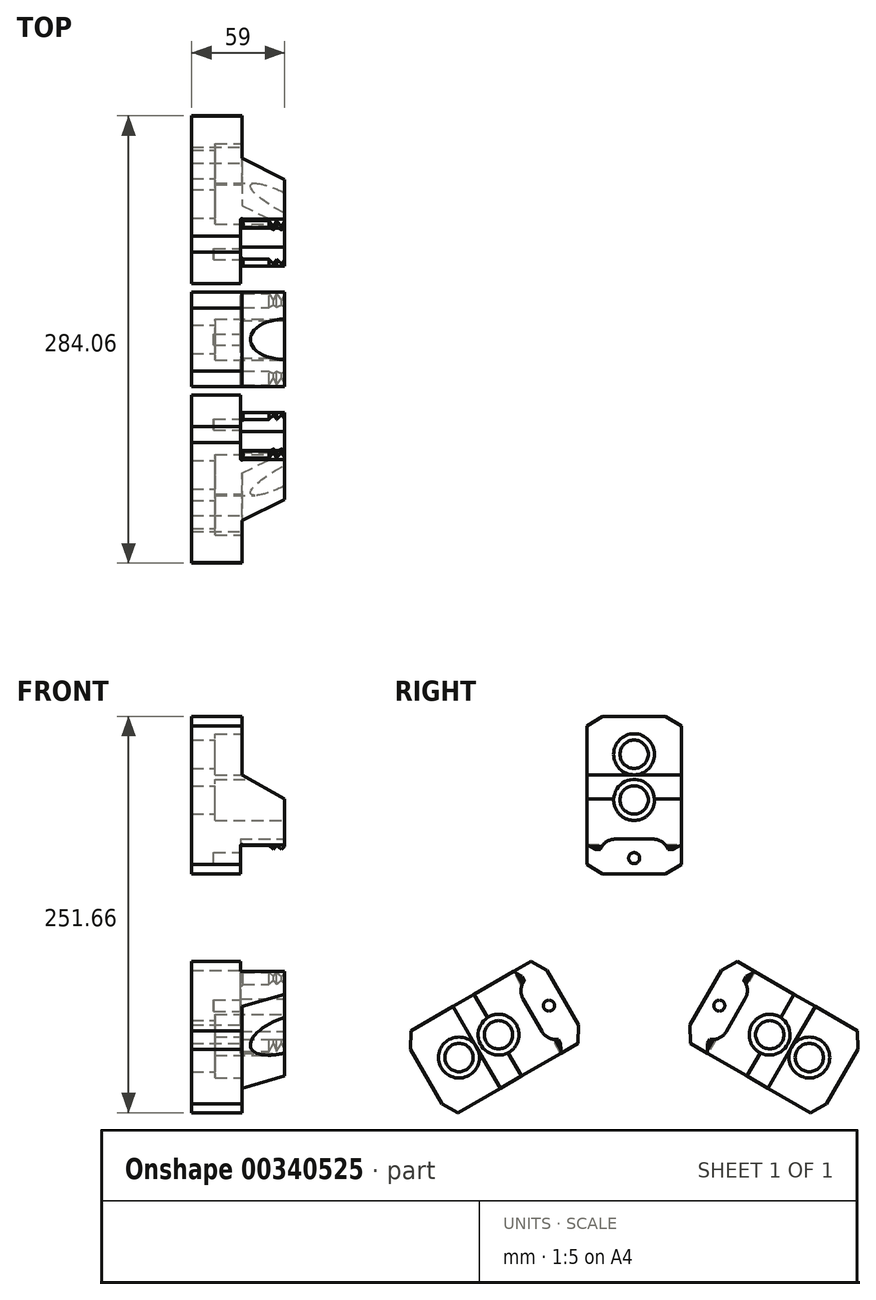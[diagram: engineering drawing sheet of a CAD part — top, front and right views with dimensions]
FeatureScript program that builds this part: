
annotation { "Feature Type Name" : "Feature", "Feature Type Description" : "" }
export const myFeature = defineFeature(function(context is Context, id is Id, definition is map)
    precondition{}
    {
        {
            var Q0;
            Q0=qCreatedBy(makeId("Front.planeOp"),FACE);
            var sketch = newSketch(context, id + "F0", { "sketchPlane" : qUnion([Q0])});
            skLineSegment(sketch, "E0", {"start": v(3, 52.45) * mm, "end": v(3, 152.45) * mm});
            skLineSegment(sketch, "E1", {"start": v(3, 152.45) * mm, "end": v(35, 152.45) * mm});
            skLineSegment(sketch, "E2", {"start": v(35, 152.45) * mm, "end": v(35, 115.45) * mm});
            skLineSegment(sketch, "E3", {"start": v(35, 115.45) * mm, "end": v(62, 100) * mm});
            skLineSegment(sketch, "E4", {"start": v(62, 100) * mm, "end": v(62, 70) * mm});
            skLineSegment(sketch, "E5", {"start": v(3, 52.45) * mm, "end": v(34, 52.45) * mm});
            skLineSegment(sketch, "E6", {"start": v(34, 52.45) * mm, "end": v(34, 70.45) * mm});
            skLineSegment(sketch, "E7", {"start": v(52, 70.45) * mm, "end": v(55, 68) * mm});
            skLineSegment(sketch, "E8", {"start": v(55, 68) * mm, "end": v(57, 70.45) * mm});
            skLineSegment(sketch, "E9", {"start": v(57, 70.45) * mm, "end": v(60, 68) * mm});
            skLineSegment(sketch, "E10", {"start": v(60, 68) * mm, "end": v(62, 70) * mm});
            skArc(sketch, "E11", {"start": v(35.5, 70.45) * mm, "mid": v(34.75, 71.2) * mm, "end": v(34, 70.45) * mm});
            skLineSegment(sketch, "E12.trimOffspring", {"start": v(35.5, 70.45) * mm, "end": v(52, 70.45) * mm});
            skLineSegment(sketch, "E13", {"start": v(0, 0) * mm, "end": v(70.08, 0) * mm, "construction": true});
            skSolve(sketch);
        }
        {
            var Q0;
            Q0=qSketchRegion(id+"F0",true);
            extrude(context, id + "F1", {"entities" : qUnion([Q0]), "endBound" : BoundingType.SYMMETRIC, "depth" : 60 * mm});
        }
        {
            var Q0;
            Q0=makeQuery(id+"F1.opExtrude","SWEPT_FACE",FACE,{"disambiguationData":[OSD([sQuery(id+"F0.wireOp",EDGE,"E2")])]});
            var sketch = newSketch(context, id + "F2", { "sketchPlane" : qUnion([Q0])});
            skLineSegment(sketch, "E14", {"start": v(20, 152.45) * mm, "end": v(30, 146.45) * mm});
            skLineSegment(sketch, "E15", {"start": v(30, 146.45) * mm, "end": v(30, 152.45) * mm});
            skLineSegment(sketch, "E16", {"start": v(30, 152.45) * mm, "end": v(20, 152.45) * mm});
            skLineSegment(sketch, "E17", {"start": v(20, 52.45) * mm, "end": v(30, 58.45) * mm});
            skLineSegment(sketch, "E18", {"start": v(30, 58.45) * mm, "end": v(30, 52.45) * mm});
            skLineSegment(sketch, "E19", {"start": v(30, 52.45) * mm, "end": v(20, 52.45) * mm});
            skLineSegment(sketch, "E20", {"start": v(0, 42.7) * mm, "end": v(0, 168.17) * mm, "construction": true});
            skLineSegment(sketch, "E21.MirrorCS", {"start": v(-20, 152.45) * mm, "end": v(-30, 146.45) * mm});
            skLineSegment(sketch, "E22.MirrorCS", {"start": v(-30, 152.45) * mm, "end": v(-20, 152.45) * mm});
            skLineSegment(sketch, "E23.MirrorCS", {"start": v(-30, 146.45) * mm, "end": v(-30, 152.45) * mm});
            skLineSegment(sketch, "E24.MirrorCS", {"start": v(-20, 52.45) * mm, "end": v(-30, 58.45) * mm});
            skLineSegment(sketch, "E25.MirrorCS", {"start": v(-30, 58.45) * mm, "end": v(-30, 52.45) * mm});
            skLineSegment(sketch, "E26.MirrorCS", {"start": v(-30, 52.45) * mm, "end": v(-20, 52.45) * mm});
            skSolve(sketch);
        }
        {
            var Q0;
            Q0=makeQuery(id+"F2.imprint","IMPRINT",FACE,{"disambiguationData":[TD([[makeQuery(id+"F2.imprint","IMPRINT",EDGE,{"derivedFrom":sQuery(id+"F2.wireOp",EDGE,"E21.MirrorCS")}),-1.0]])]});
            var Q1;
            Q1=makeQuery(id+"F2.imprint","IMPRINT",FACE,{"disambiguationData":[TD([[makeQuery(id+"F2.imprint","IMPRINT",EDGE,{"derivedFrom":sQuery(id+"F2.wireOp",EDGE,"E14")}),1.0]])]});
            var Q2;
            Q2=makeQuery(id+"F2.imprint","IMPRINT",FACE,{"disambiguationData":[TD([[makeQuery(id+"F2.imprint","IMPRINT",EDGE,{"derivedFrom":sQuery(id+"F2.wireOp",EDGE,"E17")}),-1.0]])]});
            var Q3;
            Q3=makeQuery(id+"F2.imprint","IMPRINT",FACE,{"disambiguationData":[TD([[makeQuery(id+"F2.imprint","IMPRINT",EDGE,{"derivedFrom":sQuery(id+"F2.wireOp",EDGE,"E24.MirrorCS")}),1.0]])]});
            var Q4;
            Q4=makeQuery(id+"F1.opExtrude","SWEPT_FACE",FACE,{"disambiguationData":[OSD([sQuery(id+"F0.wireOp",EDGE,"E0")])]});
            extrude(context, id + "F3", {"entities" : qUnion([Q0, Q1, Q2, Q3]), "operationType" : NewBodyOperationType.REMOVE, "endBound" : BoundingType.UP_TO_SURFACE, "oppositeDirection" : true, "endBoundEntityFace" : qUnion([Q4]), "depth" : 25 * mm});
        }
        {
            var Q0;
            Q0=makeQuery(id+"F1.opExtrude","SWEPT_FACE",FACE,{"disambiguationData":[OSD([sQuery(id+"F0.wireOp",EDGE,"E4")])]});
            var sketch = newSketch(context, id + "F4", { "sketchPlane" : qUnion([Q0])});
            skLineSegment(sketch, "E27", {"start": v(30, 71) * mm, "end": v(24.5, 68) * mm});
            skLineSegment(sketch, "E28", {"start": v(24.5, 68) * mm, "end": v(30, 68) * mm});
            skLineSegment(sketch, "E29", {"start": v(30, 68) * mm, "end": v(30, 71) * mm});
            skLineSegment(sketch, "E30", {"start": v(0, 67.05) * mm, "end": v(0, 113.15) * mm, "construction": true});
            skPoint(sketch, "E30.endSnap0", {"position": v(0, 100) * mm});
            skLineSegment(sketch, "E31.MirrorCS", {"start": v(-30, 71) * mm, "end": v(-24.5, 68) * mm});
            skLineSegment(sketch, "E32.MirrorCS", {"start": v(-30, 68) * mm, "end": v(-30, 71) * mm});
            skLineSegment(sketch, "E33.MirrorCS", {"start": v(-24.5, 68) * mm, "end": v(-30, 68) * mm});
            skSolve(sketch);
        }
        {
            var Q0;
            {var subQ0=sQuery(id+"F4.wireOp",EDGE,"E33.MirrorCS");Q0=makeQuery(id+"F4.imprint","IMPRINT",FACE,{"disambiguationData":[TD([[makeQuery(id+"F4.imprint","IMPRINT",EDGE,{"derivedFrom":subQ0}),-1.0]])]});}
            var Q1;
            {var subQ0=sQuery(id+"F4.wireOp",EDGE,"E32.MirrorCS");var subQ1=sQuery(id+"F4.wireOp",EDGE,"E31.MirrorCS");var subQ2=sQuery(id+"F0.wireOp",EDGE,"E4");var subQ3=makeQuery(id+"F4.imprint","INTERSECT",VERTEX,{"derivedFrom":[makeQuery(id+"F1.opExtrude","CAP_EDGE",EDGE,{"disambiguationData":[OSD([subQ2])],"isStart":false}),subQ1,subQ0]});Q1=makeQuery(id+"F4.imprint","IMPRINT",FACE,{"disambiguationData":[TD([[makeQuery(id+"F4.imprint","IMPRINT",EDGE,{"disambiguationData":[TD([[subQ3,-1.0]])],"derivedFrom":subQ1}),-1.0]])]});}
            var Q2;
            {var subQ0=sQuery(id+"F4.wireOp",EDGE,"E29");var subQ1=sQuery(id+"F4.wireOp",EDGE,"E27");var subQ2=sQuery(id+"F0.wireOp",EDGE,"E4");var subQ3=makeQuery(id+"F4.imprint","INTERSECT",VERTEX,{"derivedFrom":[makeQuery(id+"F1.opExtrude","CAP_EDGE",EDGE,{"disambiguationData":[OSD([subQ2])],"isStart":true}),subQ1,subQ0]});Q2=makeQuery(id+"F4.imprint","IMPRINT",FACE,{"disambiguationData":[TD([[makeQuery(id+"F4.imprint","IMPRINT",EDGE,{"disambiguationData":[TD([[subQ3,-1.0]])],"derivedFrom":subQ1}),1.0]])]});}
            var Q3;
            {var subQ0=sQuery(id+"F4.wireOp",EDGE,"E28");Q3=makeQuery(id+"F4.imprint","IMPRINT",FACE,{"disambiguationData":[TD([[makeQuery(id+"F4.imprint","IMPRINT",EDGE,{"derivedFrom":subQ0}),1.0]])]});}
            var Q4;
            Q4=makeQuery(id+"F1.opExtrude","SWEPT_FACE",FACE,{"disambiguationData":[OSD([sQuery(id+"F0.wireOp",EDGE,"E6")])]});
            extrude(context, id + "F5", {"entities" : qUnion([Q0, Q1, Q2, Q3]), "operationType" : NewBodyOperationType.REMOVE, "endBound" : BoundingType.UP_TO_SURFACE, "oppositeDirection" : true, "endBoundEntityFace" : qUnion([Q4]), "depth" : 27.7 * mm});
        }
        {
            var Q0;
            Q0=makeQuery(id+"F1.opExtrude","SWEPT_FACE",FACE,{"disambiguationData":[OSD([sQuery(id+"F0.wireOp",EDGE,"E4")])]});
            var sketch = newSketch(context, id + "F6", { "sketchPlane" : qUnion([Q0])});
            skLineSegment(sketch, "E34", {"start": v(0, 70.5) * mm, "end": v(0, 96.88) * mm, "construction": true});
            skPoint(sketch, "E34.startSnap0", {"position": v(0, 70) * mm});
            skLineSegment(sketch, "E35", {"start": v(12.26, 74.5) * mm, "end": v(0, 74.5) * mm});
            skLineSegment(sketch, "E36", {"start": v(21.5, 68) * mm, "end": v(0, 68) * mm});
            skPoint(sketch, "E37", {"position": v(12, 74.5) * mm});
            skArc(sketch, "E38", {"start": v(21.5, 68) * mm, "mid": v(17.78, 72.75) * mm, "end": v(12, 74.5) * mm});
            skPoint(sketch, "E39.end.orphan", {"position": v(21.5, 74.5) * mm});
            skLineSegment(sketch, "E40.MirrorCS", {"start": v(-12.26, 74.5) * mm, "end": v(0, 74.5) * mm});
            skArc(sketch, "E41.MirrorCS", {"start": v(-21.5, 68) * mm, "mid": v(-17.78, 72.75) * mm, "end": v(-12, 74.5) * mm});
            skLineSegment(sketch, "E42.MirrorCS", {"start": v(-21.5, 68) * mm, "end": v(0, 68) * mm});
            skSolve(sketch);
        }
        {
            var Q0;
            Q0=qSketchRegion(id+"F6",true);
            var Q1;
            {var subQ0=sQuery(id+"F0.wireOp",EDGE,"E6");Q1=makeQuery(id+"F5.boolean.opBoolean","MERGE",FACE,{"derivedFrom":[makeQuery(id+"F1.opExtrude","SWEPT_FACE",FACE,{"disambiguationData":[OSD([subQ0])]}),makeQuery(id+"F5.opExtrude","CAP_FACE",FACE,{"disambiguationData":[OSD([subQ0]),ownerDisambiguation([makeQuery(id+"F5.opExtrude","SWEPT_BODY",BODY,{"disambiguationData":[OSD([sQuery(id+"F4.wireOp",EDGE,"E27"),sQuery(id+"F4.wireOp",EDGE,"E28"),sQuery(id+"F4.wireOp",EDGE,"E29")])]})])],"isStart":false}),makeQuery(id+"F5.opExtrude","CAP_FACE",FACE,{"disambiguationData":[OSD([subQ0]),ownerDisambiguation([makeQuery(id+"F5.opExtrude","SWEPT_BODY",BODY,{"disambiguationData":[OSD([sQuery(id+"F4.wireOp",EDGE,"E31.MirrorCS"),sQuery(id+"F4.wireOp",EDGE,"E32.MirrorCS"),sQuery(id+"F4.wireOp",EDGE,"E33.MirrorCS")])]})])],"isStart":false})]});}
            extrude(context, id + "F7", {"entities" : qUnion([Q0]), "operationType" : NewBodyOperationType.REMOVE, "endBound" : BoundingType.UP_TO_SURFACE, "oppositeDirection" : true, "endBoundEntityFace" : qUnion([Q1]), "depth" : 25 * mm});
        }
        {
            var Q0;
            {var subQ0=sQuery(id+"F0.wireOp",EDGE,"E6");Q0=makeQuery(id+"F7.boolean.opBoolean","MERGE",FACE,{"derivedFrom":[makeQuery(id+"F5.boolean.opBoolean","MERGE",FACE,{"derivedFrom":[makeQuery(id+"F1.opExtrude","SWEPT_FACE",FACE,{"disambiguationData":[OSD([subQ0])]}),makeQuery(id+"F5.opExtrude","CAP_FACE",FACE,{"disambiguationData":[OSD([subQ0]),ownerDisambiguation([makeQuery(id+"F5.opExtrude","SWEPT_BODY",BODY,{"disambiguationData":[OSD([sQuery(id+"F4.wireOp",EDGE,"E27"),sQuery(id+"F4.wireOp",EDGE,"E28"),sQuery(id+"F4.wireOp",EDGE,"E29")])]})])],"isStart":false}),makeQuery(id+"F5.opExtrude","CAP_FACE",FACE,{"disambiguationData":[OSD([subQ0]),ownerDisambiguation([makeQuery(id+"F5.opExtrude","SWEPT_BODY",BODY,{"disambiguationData":[OSD([sQuery(id+"F4.wireOp",EDGE,"E31.MirrorCS"),sQuery(id+"F4.wireOp",EDGE,"E32.MirrorCS"),sQuery(id+"F4.wireOp",EDGE,"E33.MirrorCS")])]})])],"isStart":false})]}),makeQuery(id+"F7.opExtrude","CAP_FACE",FACE,{"disambiguationData":[OSD([subQ0])],"isStart":false})]});}
            var sketch = newSketch(context, id + "F8", { "sketchPlane" : qUnion([Q0])});
            skCircle(sketch, "E43.cCircle", {"center": v(0, 62.45) * mm, "radius": 6.5 * mm, "construction": true});
            skLineSegment(sketch, "E43.0", {"start": v(7.5, 62.45) * mm, "end": v(3.75, 55.95) * mm});
            skLineSegment(sketch, "E43.1", {"start": v(3.75, 55.95) * mm, "end": v(-3.75, 55.95) * mm});
            skLineSegment(sketch, "E43.2", {"start": v(-3.75, 55.95) * mm, "end": v(-7.5, 62.45) * mm});
            skLineSegment(sketch, "E43.3", {"start": v(-7.5, 62.45) * mm, "end": v(-3.75, 68.95) * mm});
            skLineSegment(sketch, "E43.4", {"start": v(-3.75, 68.95) * mm, "end": v(3.75, 68.95) * mm});
            skLineSegment(sketch, "E43.5", {"start": v(3.75, 68.95) * mm, "end": v(7.5, 62.45) * mm});
            skPoint(sketch, "E43.0.midPoint", {"position": v(5.63, 59.2) * mm});
            skCircle(sketch, "E44", {"center": v(0, 62.45) * mm, "radius": 3.5 * mm});
            skSolve(sketch);
        }
        {
            var Q0;
            Q0=makeQuery(id+"F8.imprint","IMPRINT",FACE,{"disambiguationData":[TD([[makeQuery(id+"F8.imprint","IMPRINT",EDGE,{"derivedFrom":sQuery(id+"F8.wireOp",EDGE,"E44")}),1.0]])]});
            extrude(context, id + "F9", {"entities" : qUnion([Q0]), "operationType" : NewBodyOperationType.REMOVE, "oppositeDirection" : true, "depth" : 17 * mm});
        }
        {
            var Q0;
            Q0=makeQuery(id+"F1.opExtrude","SWEPT_FACE",FACE,{"disambiguationData":[OSD([sQuery(id+"F0.wireOp",EDGE,"E4")])]});
            var sketch = newSketch(context, id + "F10", { "sketchPlane" : qUnion([Q0])});
            skLineSegment(sketch, "E45", {"start": v(0, 77.6) * mm, "end": v(0, 164.13) * mm, "construction": true});
            skPoint(sketch, "E45.startSnap0", {"position": v(0, 74.5) * mm});
            skCircle(sketch, "E46", {"center": v(0, 128.45) * mm, "radius": 13 * mm});
            skCircle(sketch, "E47", {"center": v(0, 99.45) * mm, "radius": 13 * mm});
            skCircle(sketch, "E48", {"center": v(0, 128.45) * mm, "radius": 9 * mm});
            skCircle(sketch, "E49", {"center": v(0, 99.45) * mm, "radius": 9 * mm});
            skSolve(sketch);
        }
        {
            var Q0;
            Q0=makeQuery(id+"F10.imprint","IMPRINT",FACE,{"disambiguationData":[TD([[makeQuery(id+"F10.imprint","IMPRINT",EDGE,{"derivedFrom":sQuery(id+"F10.wireOp",EDGE,"E48")}),1.0]])]});
            var Q1;
            {var subQ0=sQuery(id+"F10.wireOp",EDGE,"E49");var subQ1=makeQuery(id+"F1.opExtrude","SWEPT_EDGE",EDGE,{"disambiguationData":[OSD([sQuery(id+"F0.wireOp",EDGE,"E3"),sQuery(id+"F0.wireOp",EDGE,"E4")])]});var subQ2=makeQuery(id+"F10.imprint","INTERSECT",VERTEX,{"disambiguationData":[OD(0.0)],"derivedFrom":[subQ1,subQ0]});Q1=makeQuery(id+"F10.imprint","IMPRINT",FACE,{"disambiguationData":[TD([[makeQuery(id+"F10.imprint","IMPRINT",EDGE,{"disambiguationData":[TD([[subQ2,1.0]])],"derivedFrom":subQ0}),1.0]])]});}
            var Q2;
            {var subQ0=sQuery(id+"F10.wireOp",EDGE,"E49");var subQ1=makeQuery(id+"F1.opExtrude","SWEPT_EDGE",EDGE,{"disambiguationData":[OSD([sQuery(id+"F0.wireOp",EDGE,"E3"),sQuery(id+"F0.wireOp",EDGE,"E4")])]});var subQ2=makeQuery(id+"F10.imprint","INTERSECT",VERTEX,{"disambiguationData":[OD(0.0)],"derivedFrom":[subQ1,subQ0]});Q2=makeQuery(id+"F10.imprint","IMPRINT",FACE,{"disambiguationData":[TD([[makeQuery(id+"F10.imprint","IMPRINT",EDGE,{"disambiguationData":[TD([[subQ2,-1.0]])],"derivedFrom":subQ0}),1.0]])]});}
            var Q3;
            Q3=makeQuery(id+"F1.opExtrude","SWEPT_FACE",FACE,{"disambiguationData":[OSD([sQuery(id+"F0.wireOp",EDGE,"E0")])]});
            extrude(context, id + "F11", {"entities" : qUnion([Q0, Q1, Q2]), "operationType" : NewBodyOperationType.REMOVE, "endBound" : BoundingType.UP_TO_SURFACE, "oppositeDirection" : true, "endBoundEntityFace" : qUnion([Q3]), "depth" : 25 * mm});
        }
        {
            var Q0;
            Q0=makeQuery(id+"F10.imprint","IMPRINT",FACE,{"disambiguationData":[TD([[makeQuery(id+"F10.imprint","IMPRINT",EDGE,{"derivedFrom":sQuery(id+"F10.wireOp",EDGE,"E46")}),1.0]])]});
            var Q1;
            {var subQ0=sQuery(id+"F10.wireOp",EDGE,"E47");var subQ1=makeQuery(id+"F1.opExtrude","SWEPT_EDGE",EDGE,{"disambiguationData":[OSD([sQuery(id+"F0.wireOp",EDGE,"E3"),sQuery(id+"F0.wireOp",EDGE,"E4")])]});var subQ2=makeQuery(id+"F10.imprint","INTERSECT",VERTEX,{"disambiguationData":[OD(0.0)],"derivedFrom":[subQ1,subQ0]});Q1=makeQuery(id+"F10.imprint","IMPRINT",FACE,{"disambiguationData":[TD([[makeQuery(id+"F10.imprint","IMPRINT",EDGE,{"disambiguationData":[TD([[subQ2,-1.0]])],"derivedFrom":subQ0}),1.0]])]});}
            var Q2;
            {var subQ0=sQuery(id+"F10.wireOp",EDGE,"E47");var subQ1=makeQuery(id+"F1.opExtrude","SWEPT_EDGE",EDGE,{"disambiguationData":[OSD([sQuery(id+"F0.wireOp",EDGE,"E3"),sQuery(id+"F0.wireOp",EDGE,"E4")])]});var subQ2=makeQuery(id+"F10.imprint","INTERSECT",VERTEX,{"disambiguationData":[OD(0.0)],"derivedFrom":[subQ1,subQ0]});Q2=makeQuery(id+"F10.imprint","IMPRINT",FACE,{"disambiguationData":[TD([[makeQuery(id+"F10.imprint","IMPRINT",EDGE,{"disambiguationData":[TD([[subQ2,1.0]])],"derivedFrom":subQ0}),1.0]])]});}
            extrude(context, id + "F12", {"entities" : qUnion([Q0, Q1, Q2]), "operationType" : NewBodyOperationType.REMOVE, "oppositeDirection" : true, "depth" : 44 * mm});
        }
        {
            var Q0;
            Q0=makeQuery(id+"F1.opExtrude","SWEPT_BODY",BODY,{"disambiguationData":[OSD([sQuery(id+"F0.wireOp",EDGE,"E0"),sQuery(id+"F0.wireOp",EDGE,"E1"),sQuery(id+"F0.wireOp",EDGE,"E2"),sQuery(id+"F0.wireOp",EDGE,"E3"),sQuery(id+"F0.wireOp",EDGE,"E4"),sQuery(id+"F0.wireOp",EDGE,"E5"),sQuery(id+"F0.wireOp",EDGE,"E6"),sQuery(id+"F0.wireOp",EDGE,"E7"),sQuery(id+"F0.wireOp",EDGE,"E8"),sQuery(id+"F0.wireOp",EDGE,"E9"),sQuery(id+"F0.wireOp",EDGE,"E10"),sQuery(id+"F0.wireOp",EDGE,"E11"),sQuery(id+"F0.wireOp",EDGE,"E12.trimOffspring")])]});
            var Q1;
            Q1=sQuery(id+"F0.wireOp",EDGE,"E13");
            circularPattern(context, id + "F13", {"entities" : qUnion([Q0]), "axis" : qUnion([Q1]), "angle" : 360 * degree, "instanceCount" : 3, "equalSpace" : true});
        }
    });
